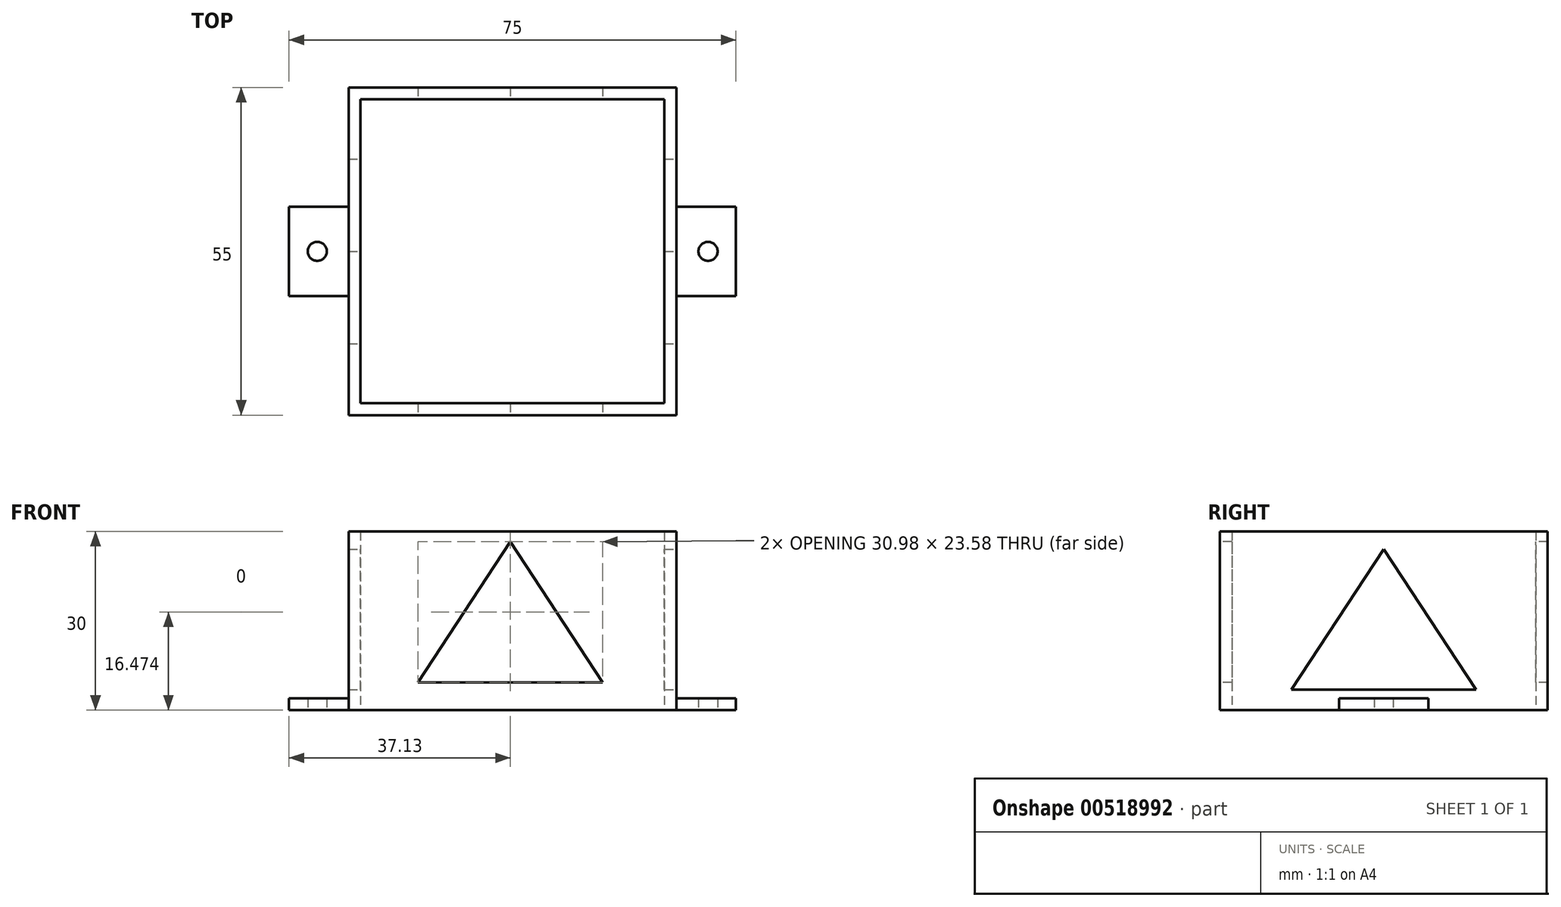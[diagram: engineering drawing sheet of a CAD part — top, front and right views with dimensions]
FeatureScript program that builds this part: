
annotation { "Feature Type Name" : "Feature", "Feature Type Description" : "" }
export const myFeature = defineFeature(function(context is Context, id is Id, definition is map)
    precondition{}
    {
        {
            var Q0;
            Q0=qCreatedBy(makeId("Top.planeOp"),FACE);
            var sketch = newSketch(context, id + "F0", { "sketchPlane" : qUnion([Q0])});
            skLineSegment(sketch, "E0.bottom", {"start": v(-26.32, 25.5) * mm, "end": v(24.68, 25.5) * mm});
            skLineSegment(sketch, "E0.top", {"start": v(-26.32, -25.5) * mm, "end": v(24.68, -25.5) * mm});
            skLineSegment(sketch, "E0.left", {"start": v(-26.32, 25.5) * mm, "end": v(-26.32, -25.5) * mm});
            skLineSegment(sketch, "E0.right", {"start": v(24.68, 25.5) * mm, "end": v(24.68, -25.5) * mm});
            skLineSegment(sketch, "E1.bottom", {"start": v(-28.32, 27.5) * mm, "end": v(26.68, 27.5) * mm});
            skLineSegment(sketch, "E1.top", {"start": v(-28.32, -27.5) * mm, "end": v(26.68, -27.5) * mm});
            skLineSegment(sketch, "E1.left", {"start": v(-28.32, 27.5) * mm, "end": v(-28.32, -27.5) * mm});
            skLineSegment(sketch, "E1.right", {"start": v(26.68, 27.5) * mm, "end": v(26.68, -27.5) * mm});
            skLineSegment(sketch, "E2", {"start": v(24.68, 0) * mm, "end": v(26.68, 0) * mm, "construction": true});
            skLineSegment(sketch, "E3", {"start": v(-26.32, 0) * mm, "end": v(-28.32, 0) * mm, "construction": true});
            skLineSegment(sketch, "E4", {"start": v(-0.82, -25.5) * mm, "end": v(-0.82, -27.5) * mm, "construction": true});
            skLineSegment(sketch, "E5", {"start": v(-0.82, 25.5) * mm, "end": v(-0.82, 27.5) * mm, "construction": true});
            skLineSegment(sketch, "E6.bottom", {"start": v(-28.32, 7.5) * mm, "end": v(-38.32, 7.5) * mm});
            skLineSegment(sketch, "E6.top", {"start": v(-28.32, -7.5) * mm, "end": v(-38.32, -7.5) * mm});
            skLineSegment(sketch, "E6.left", {"start": v(-28.32, 7.5) * mm, "end": v(-28.32, -7.5) * mm});
            skLineSegment(sketch, "E6.right", {"start": v(-38.32, 7.5) * mm, "end": v(-38.32, -7.5) * mm});
            skLineSegment(sketch, "E7.bottom", {"start": v(-7.5, -27.5) * mm, "end": v(7.5, -27.5) * mm});
            skLineSegment(sketch, "E7.top", {"start": v(-7.5, -37.5) * mm, "end": v(7.5, -37.5) * mm});
            skLineSegment(sketch, "E7.left", {"start": v(-7.5, -27.5) * mm, "end": v(-7.5, -37.5) * mm});
            skLineSegment(sketch, "E7.right", {"start": v(7.5, -27.5) * mm, "end": v(7.5, -37.5) * mm});
            skLineSegment(sketch, "E8.bottom", {"start": v(26.68, -7.5) * mm, "end": v(36.68, -7.5) * mm});
            skLineSegment(sketch, "E8.top", {"start": v(26.68, 7.5) * mm, "end": v(36.68, 7.5) * mm});
            skLineSegment(sketch, "E8.left", {"start": v(26.68, -7.5) * mm, "end": v(26.68, 7.5) * mm});
            skLineSegment(sketch, "E8.right", {"start": v(36.68, -7.5) * mm, "end": v(36.68, 7.5) * mm});
            skLineSegment(sketch, "E9.bottom", {"start": v(7.5, 27.5) * mm, "end": v(-7.5, 27.5) * mm});
            skLineSegment(sketch, "E9.top", {"start": v(7.5, 37.5) * mm, "end": v(-7.5, 37.5) * mm});
            skLineSegment(sketch, "E9.left", {"start": v(7.5, 27.5) * mm, "end": v(7.5, 37.5) * mm});
            skLineSegment(sketch, "E9.right", {"start": v(-7.5, 27.5) * mm, "end": v(-7.5, 37.5) * mm});
            skCircle(sketch, "E10", {"center": v(-33.58, 0) * mm, "radius": 1.6 * mm});
            skCircle(sketch, "E11", {"center": v(32, 0) * mm, "radius": 1.6 * mm});
            skPoint(sketch, "E11.centerSnap0", {"position": v(26.68, 0) * mm});
            skCircle(sketch, "E12", {"center": v(0, 33.88) * mm, "radius": 1.6 * mm});
            skCircle(sketch, "E13", {"center": v(0, -32.1) * mm, "radius": 1.6 * mm});
            skPoint(sketch, "E13.centerSnap0", {"position": v(0, -37.5) * mm});
            skPoint(sketch, "E14", {"position": v(36.68, 0) * mm});
            skSolve(sketch);
        }
        {
            var Q0;
            Q0=makeQuery(id+"F0.imprint","IMPRINT",FACE,{"disambiguationData":[TD([[makeQuery(id+"F0.imprint","IMPRINT",EDGE,{"derivedFrom":sQuery(id+"F0.wireOp",EDGE,"E0.bottom")}),1.0]])]});
            extrude(context, id + "F1", {"entities" : qUnion([Q0]), "depth" : 30 * mm, "offsetDistance" : 25 * mm});
        }
        {
            var Q0;
            Q0=makeQuery(id+"F0.imprint","IMPRINT",FACE,{"disambiguationData":[TD([[makeQuery(id+"F0.imprint","IMPRINT",EDGE,{"derivedFrom":sQuery(id+"F0.wireOp",EDGE,"E9.bottom")}),-1.0]])]});
            var Q1;
            Q1=makeQuery(id+"F0.imprint","IMPRINT",FACE,{"disambiguationData":[TD([[makeQuery(id+"F0.imprint","IMPRINT",EDGE,{"derivedFrom":sQuery(id+"F0.wireOp",EDGE,"E8.bottom")}),1.0]])]});
            var Q2;
            Q2=makeQuery(id+"F0.imprint","IMPRINT",FACE,{"disambiguationData":[TD([[makeQuery(id+"F0.imprint","IMPRINT",EDGE,{"derivedFrom":sQuery(id+"F0.wireOp",EDGE,"E7.bottom")}),-1.0]])]});
            var Q3;
            Q3=makeQuery(id+"F0.imprint","IMPRINT",FACE,{"disambiguationData":[TD([[makeQuery(id+"F0.imprint","IMPRINT",EDGE,{"derivedFrom":sQuery(id+"F0.wireOp",EDGE,"E6.bottom")}),1.0]])]});
            extrude(context, id + "F2", {"entities" : qUnion([Q0, Q1, Q2, Q3]), "operationType" : NewBodyOperationType.ADD, "depth" : 2 * mm, "offsetDistance" : 25 * mm});
        }
        {
            var Q0;
            Q0=makeQuery(id+"F1.opExtrude","SWEPT_FACE",FACE,{"disambiguationData":[OSD([sQuery(id+"F0.wireOp",EDGE,"E1.right"),sQuery(id+"F0.wireOp",EDGE,"E8.left")])]});
            var sketch = newSketch(context, id + "F3", { "sketchPlane" : qUnion([Q0])});
            skLineSegment(sketch, "E15", {"start": v(0, 27.04) * mm, "end": v(-15.49, 3.46) * mm});
            skLineSegment(sketch, "E16", {"start": v(-15.49, 3.46) * mm, "end": v(15.49, 3.46) * mm});
            skLineSegment(sketch, "E17", {"start": v(15.49, 3.46) * mm, "end": v(0, 27.04) * mm});
            skSolve(sketch);
        }
        {
            var Q0;
            Q0=makeQuery(id+"F3.imprint","IMPRINT",FACE,{"disambiguationData":[TD([[makeQuery(id+"F3.imprint","IMPRINT",EDGE,{"derivedFrom":sQuery(id+"F3.wireOp",EDGE,"E15")}),1.0]])]});
            extrude(context, id + "F4", {"entities" : qUnion([Q0]), "operationType" : NewBodyOperationType.REMOVE, "oppositeDirection" : true, "depth" : 100 * mm, "offsetDistance" : 25 * mm});
        }
        {
            var Q0;
            Q0=makeQuery(id+"F1.opExtrude","SWEPT_FACE",FACE,{"disambiguationData":[OSD([sQuery(id+"F0.wireOp",EDGE,"E1.top"),sQuery(id+"F0.wireOp",EDGE,"E7.bottom")])]});
            var sketch = newSketch(context, id + "F5", { "sketchPlane" : qUnion([Q0])});
            skLineSegment(sketch, "E18", {"start": v(-1.19, 28.26) * mm, "end": v(-16.68, 4.69) * mm});
            skLineSegment(sketch, "E19", {"start": v(-16.68, 4.69) * mm, "end": v(14.3, 4.69) * mm});
            skLineSegment(sketch, "E20", {"start": v(14.3, 4.69) * mm, "end": v(-1.19, 28.26) * mm});
            skSolve(sketch);
        }
        {
            var Q0;
            Q0=makeQuery(id+"F5.imprint","IMPRINT",FACE,{"disambiguationData":[TD([[makeQuery(id+"F5.imprint","IMPRINT",EDGE,{"derivedFrom":sQuery(id+"F5.wireOp",EDGE,"E18")}),1.0]])]});
            extrude(context, id + "F6", {"entities" : qUnion([Q0]), "operationType" : NewBodyOperationType.REMOVE, "oppositeDirection" : true, "depth" : 100 * mm, "offsetDistance" : 25 * mm});
        }
    });
